# Revit family: SINK_PRIMARY
name_source: partatom
category: Furniture
units: mm (PartAtom-declared; Revit-internal decimal feet)

## family parameters
Always vertical = Yes
Cut with Voids When Loaded = No
OmniClass Number = 23.40.20.00
OmniClass Title = General Furniture and Specialties
Room Calculation Point = No
Shared = No
Work Plane-Based = No

## types (33) — shared parameters
FULL_WT = Yes
HEIGHT = 900 mm  [stored 2.95276 ft]
LOW_TAG = No
Manufacturer = IBR InnovaSystem
URL = https://ibr-innovasystem.com
zero-valued in all types: Default Elevation

## per-type parameters (varying)
| type | 1DOOR | 2DOOR | 3DOOR | ANCHO_FREG | DRBOWLW | DRBWL | DRBWR | DRNEUTW | DRNTL | DRNTR | Description | FRAMEW | FREG_CN | FREG_DC | FREG_IZ | HANDLEXB | HANDLEXN | POSBOWDRL | POSBOWDRR | POSNEUTL | POSNEUTR | POS_FREG | WIDTH | depth |
| SKPR-1575L | No | No | Yes | 500 mm  [stored 1.64042 ft] | 440 mm  [stored 1.44357 ft] | Yes | Yes | 587 mm | No | Yes | Primary Sink 1500x750, Bowl at Left side | 1468 mm  [stored 4.81627 ft] | No | No | Yes | 74 mm | 148 mm | 0 mm  [stored 0 ft] | 587 mm | 0 mm  [stored 0 ft] | 0 mm  [stored 0 ft] | 350 mm  [stored 1.14829 ft] | 1500 mm  [stored 4.92126 ft] | 750 mm  [stored 2.46063 ft] |
| SKPR-1575R | No | No | Yes | 500 mm  [stored 1.64042 ft] | 440 mm  [stored 1.44357 ft] | Yes | Yes | 587 mm | Yes | No | Primary Sink 1500x750, Bowl at Right side | 1468 mm  [stored 4.81627 ft] | No | Yes | No | 74 mm | 148 mm | 587 mm | 0 mm  [stored 0 ft] | 0 mm  [stored 0 ft] | 0 mm  [stored 0 ft] | 1150 mm | 1500 mm  [stored 4.92126 ft] | 750 mm  [stored 2.46063 ft] |
| SKPR-1575C | No | No | Yes | 500 mm  [stored 1.64042 ft] | 440 mm  [stored 1.44357 ft] | Yes | Yes | 587 mm | No | Yes | Primary Sink 1500x750, Bowl at Center | 1468 mm  [stored 4.81627 ft] | Yes | No | No | 74 mm | 148 mm | 0 mm  [stored 0 ft] | 0 mm  [stored 0 ft] | 440 mm  [stored 1.44357 ft] | 440 mm  [stored 1.44357 ft] | 750 mm  [stored 2.46063 ft] | 1500 mm  [stored 4.92126 ft] | 750 mm  [stored 2.46063 ft] |
| SKPR-1560R | No | No | Yes | 500 mm  [stored 1.64042 ft] | 440 mm  [stored 1.44357 ft] | Yes | Yes | 587 mm | Yes | No | Primary Sink 1500x600, Bowl at Right side | 1468 mm  [stored 4.81627 ft] | No | Yes | No | 74 mm | 148 mm | 587 mm | 0 mm  [stored 0 ft] | 0 mm  [stored 0 ft] | 0 mm  [stored 0 ft] | 1150 mm | 1500 mm  [stored 4.92126 ft] | 600 mm  [stored 1.9685 ft] |
| SKPR-1560L | No | No | Yes | 500 mm  [stored 1.64042 ft] | 440 mm  [stored 1.44357 ft] | Yes | Yes | 587 mm | No | Yes | Primary Sink 1500x600, Bowl at Left side | 1468 mm  [stored 4.81627 ft] | No | No | Yes | 74 mm | 148 mm | 0 mm  [stored 0 ft] | 587 mm | 0 mm  [stored 0 ft] | 0 mm  [stored 0 ft] | 350 mm  [stored 1.14829 ft] | 1500 mm  [stored 4.92126 ft] | 600 mm  [stored 1.9685 ft] |
| SKPR-1560C | No | No | Yes | 500 mm  [stored 1.64042 ft] | 440 mm  [stored 1.44357 ft] | Yes | Yes | 587 mm | No | Yes | Primary Sink 1500x600, Bowl at Center | 1468 mm  [stored 4.81627 ft] | Yes | No | No | 74 mm | 148 mm | 0 mm  [stored 0 ft] | 0 mm  [stored 0 ft] | 440 mm  [stored 1.44357 ft] | 440 mm  [stored 1.44357 ft] | 750 mm  [stored 2.46063 ft] | 1500 mm  [stored 4.92126 ft] | 600 mm  [stored 1.9685 ft] |
| SKPR-1590C | No | No | Yes | 500 mm  [stored 1.64042 ft] | 440 mm  [stored 1.44357 ft] | Yes | Yes | 587 mm | No | Yes | Primary Sink 1500x900, Bowl at Center | 1468 mm  [stored 4.81627 ft] | Yes | No | No | 74 mm | 148 mm | 0 mm  [stored 0 ft] | 0 mm  [stored 0 ft] | 440 mm  [stored 1.44357 ft] | 440 mm  [stored 1.44357 ft] | 750 mm  [stored 2.46063 ft] | 1500 mm  [stored 4.92126 ft] | 900 mm  [stored 2.95276 ft] |
| SKPR-1590L | No | No | Yes | 500 mm  [stored 1.64042 ft] | 440 mm  [stored 1.44357 ft] | Yes | Yes | 587 mm | No | Yes | Primary Sink 1500x900, Bowl at Left side | 1468 mm  [stored 4.81627 ft] | No | No | Yes | 74 mm | 148 mm | 0 mm  [stored 0 ft] | 587 mm | 0 mm  [stored 0 ft] | 0 mm  [stored 0 ft] | 350 mm  [stored 1.14829 ft] | 1500 mm  [stored 4.92126 ft] | 900 mm  [stored 2.95276 ft] |
| SKPR-1590R | No | No | Yes | 500 mm  [stored 1.64042 ft] | 440 mm  [stored 1.44357 ft] | Yes | Yes | 587 mm | Yes | No | Primary Sink 1500x900, Bowl at Right side | 1468 mm  [stored 4.81627 ft] | No | Yes | No | 74 mm | 148 mm | 587 mm | 0 mm  [stored 0 ft] | 0 mm  [stored 0 ft] | 0 mm  [stored 0 ft] | 1150 mm | 1500 mm  [stored 4.92126 ft] | 900 mm  [stored 2.95276 ft] |
| SKPR-1275L | No | Yes | No | 500 mm  [stored 1.64042 ft] | 584 mm  [stored 1.91601 ft] | Yes | Yes | 600 mm  [stored 1.9685 ft] | No | No | Primary Sink 1200x750, Bowl at Left side | 1168 mm  [stored 3.83202 ft] | No | No | Yes | 146 mm  [stored 0.479003 ft] | 154 mm  [stored 0.505249 ft] | 0 mm  [stored 0 ft] | 0 mm  [stored 0 ft] | 0 mm  [stored 0 ft] | 0 mm  [stored 0 ft] | 350 mm  [stored 1.14829 ft] | 1200 mm  [stored 3.93701 ft] | 750 mm  [stored 2.46063 ft] |
| SKPR-1275R | No | Yes | No | 500 mm  [stored 1.64042 ft] | 584 mm  [stored 1.91601 ft] | Yes | Yes | 600 mm  [stored 1.9685 ft] | No | No | Primary Sink 1200x750, Bowl at Right side | 1168 mm  [stored 3.83202 ft] | No | Yes | No | 146 mm  [stored 0.479003 ft] | 154 mm  [stored 0.505249 ft] | 0 mm  [stored 0 ft] | 0 mm  [stored 0 ft] | 0 mm  [stored 0 ft] | 0 mm  [stored 0 ft] | 850 mm  [stored 2.78871 ft] | 1200 mm  [stored 3.93701 ft] | 750 mm  [stored 2.46063 ft] |
| SKPR-1275C | No | Yes | No | 500 mm  [stored 1.64042 ft] | 584 mm  [stored 1.91601 ft] | Yes | Yes | 600 mm  [stored 1.9685 ft] | No | No | Primary Sink 1200x750, Bowl at Center | 1168 mm  [stored 3.83202 ft] | Yes | No | No | 146 mm  [stored 0.479003 ft] | 154 mm  [stored 0.505249 ft] | 0 mm  [stored 0 ft] | 0 mm  [stored 0 ft] | 0 mm  [stored 0 ft] | 0 mm  [stored 0 ft] | 600 mm  [stored 1.9685 ft] | 1200 mm  [stored 3.93701 ft] | 750 mm  [stored 2.46063 ft] |
| SKPR-1260C | No | Yes | No | 500 mm  [stored 1.64042 ft] | 584 mm  [stored 1.91601 ft] | Yes | Yes | 600 mm  [stored 1.9685 ft] | No | No | Primary Sink 1200x600, Bowl at Center | 1168 mm  [stored 3.83202 ft] | Yes | No | No | 146 mm  [stored 0.479003 ft] | 154 mm  [stored 0.505249 ft] | 0 mm  [stored 0 ft] | 0 mm  [stored 0 ft] | 0 mm  [stored 0 ft] | 0 mm  [stored 0 ft] | 600 mm  [stored 1.9685 ft] | 1200 mm  [stored 3.93701 ft] | 600 mm  [stored 1.9685 ft] |
| SKPR-1260L | No | Yes | No | 500 mm  [stored 1.64042 ft] | 584 mm  [stored 1.91601 ft] | Yes | Yes | 600 mm  [stored 1.9685 ft] | No | No | Primary Sink 1200x600, Bowl at Left side | 1168 mm  [stored 3.83202 ft] | No | No | Yes | 146 mm  [stored 0.479003 ft] | 154 mm  [stored 0.505249 ft] | 0 mm  [stored 0 ft] | 0 mm  [stored 0 ft] | 0 mm  [stored 0 ft] | 0 mm  [stored 0 ft] | 350 mm  [stored 1.14829 ft] | 1200 mm  [stored 3.93701 ft] | 600 mm  [stored 1.9685 ft] |
| SKPR-1260R | No | Yes | No | 500 mm  [stored 1.64042 ft] | 584 mm  [stored 1.91601 ft] | Yes | Yes | 600 mm  [stored 1.9685 ft] | No | No | Primary Sink 1200x600, Bowl at Right side | 1168 mm  [stored 3.83202 ft] | No | Yes | No | 146 mm  [stored 0.479003 ft] | 154 mm  [stored 0.505249 ft] | 0 mm  [stored 0 ft] | 0 mm  [stored 0 ft] | 0 mm  [stored 0 ft] | 0 mm  [stored 0 ft] | 850 mm  [stored 2.78871 ft] | 1200 mm  [stored 3.93701 ft] | 600 mm  [stored 1.9685 ft] |
| SKPR-1290R | No | Yes | No | 500 mm  [stored 1.64042 ft] | 584 mm  [stored 1.91601 ft] | Yes | Yes | 600 mm  [stored 1.9685 ft] | No | No | Primary Sink 1200x900, Bowl at Right side | 1168 mm  [stored 3.83202 ft] | No | Yes | No | 146 mm  [stored 0.479003 ft] | 154 mm  [stored 0.505249 ft] | 0 mm  [stored 0 ft] | 0 mm  [stored 0 ft] | 0 mm  [stored 0 ft] | 0 mm  [stored 0 ft] | 850 mm  [stored 2.78871 ft] | 1200 mm  [stored 3.93701 ft] | 900 mm  [stored 2.95276 ft] |
| SKPR-1290L | No | Yes | No | 500 mm  [stored 1.64042 ft] | 584 mm  [stored 1.91601 ft] | Yes | Yes | 600 mm  [stored 1.9685 ft] | No | No | Primary Sink 1200x900, Bowl at Left side | 1168 mm  [stored 3.83202 ft] | No | No | Yes | 146 mm  [stored 0.479003 ft] | 154 mm  [stored 0.505249 ft] | 0 mm  [stored 0 ft] | 0 mm  [stored 0 ft] | 0 mm  [stored 0 ft] | 0 mm  [stored 0 ft] | 350 mm  [stored 1.14829 ft] | 1200 mm  [stored 3.93701 ft] | 900 mm  [stored 2.95276 ft] |
| SKPR-1290C | No | Yes | No | 500 mm  [stored 1.64042 ft] | 584 mm  [stored 1.91601 ft] | Yes | Yes | 600 mm  [stored 1.9685 ft] | No | No | Primary Sink 1200x900, Bowl at Center | 1168 mm  [stored 3.83202 ft] | Yes | No | No | 146 mm  [stored 0.479003 ft] | 154 mm  [stored 0.505249 ft] | 0 mm  [stored 0 ft] | 0 mm  [stored 0 ft] | 0 mm  [stored 0 ft] | 0 mm  [stored 0 ft] | 600 mm  [stored 1.9685 ft] | 1200 mm  [stored 3.93701 ft] | 900 mm  [stored 2.95276 ft] |
| SKPR-0975R | No | Yes | No | 400 mm  [stored 1.31234 ft] | 434 mm  [stored 1.42388 ft] | Yes | Yes | 600 mm  [stored 1.9685 ft] | No | No | Primary Sink 900x750, Bowl at Right side | 868 mm  [stored 2.84777 ft] | No | Yes | No | 71 mm  [stored 0.23294 ft] | 154 mm  [stored 0.505249 ft] | 0 mm  [stored 0 ft] | 0 mm  [stored 0 ft] | 0 mm  [stored 0 ft] | 0 mm  [stored 0 ft] | 600 mm  [stored 1.9685 ft] | 900 mm  [stored 2.95276 ft] | 750 mm  [stored 2.46063 ft] |
| SKPR-0975L | No | Yes | No | 400 mm  [stored 1.31234 ft] | 434 mm  [stored 1.42388 ft] | Yes | Yes | 600 mm  [stored 1.9685 ft] | No | No | Primary Sink 900x750, Bowl at Left side | 868 mm  [stored 2.84777 ft] | No | No | Yes | 71 mm  [stored 0.23294 ft] | 154 mm  [stored 0.505249 ft] | 0 mm  [stored 0 ft] | 0 mm  [stored 0 ft] | 0 mm  [stored 0 ft] | 0 mm  [stored 0 ft] | 300 mm  [stored 0.984252 ft] | 900 mm  [stored 2.95276 ft] | 750 mm  [stored 2.46063 ft] |
| SKPR-0975C | No | Yes | No | 400 mm  [stored 1.31234 ft] | 434 mm  [stored 1.42388 ft] | Yes | Yes | 600 mm  [stored 1.9685 ft] | No | No | Primary Sink 900x750, Bowl at Center | 868 mm  [stored 2.84777 ft] | Yes | No | No | 71 mm  [stored 0.23294 ft] | 154 mm  [stored 0.505249 ft] | 0 mm  [stored 0 ft] | 0 mm  [stored 0 ft] | 0 mm  [stored 0 ft] | 0 mm  [stored 0 ft] | 450 mm  [stored 1.47638 ft] | 900 mm  [stored 2.95276 ft] | 750 mm  [stored 2.46063 ft] |
| SKPR-0960C | No | Yes | No | 400 mm  [stored 1.31234 ft] | 434 mm  [stored 1.42388 ft] | Yes | Yes | 600 mm  [stored 1.9685 ft] | No | No | Primary Sink 900x600, Bowl at Center | 868 mm  [stored 2.84777 ft] | Yes | No | No | 71 mm  [stored 0.23294 ft] | 154 mm  [stored 0.505249 ft] | 0 mm  [stored 0 ft] | 0 mm  [stored 0 ft] | 0 mm  [stored 0 ft] | 0 mm  [stored 0 ft] | 450 mm  [stored 1.47638 ft] | 900 mm  [stored 2.95276 ft] | 750 mm  [stored 2.46063 ft] |
| SKPR-0960R | No | Yes | No | 400 mm  [stored 1.31234 ft] | 434 mm  [stored 1.42388 ft] | Yes | Yes | 600 mm  [stored 1.9685 ft] | No | No | Primary Sink 900x600, Bowl at Right side | 868 mm  [stored 2.84777 ft] | No | Yes | No | 71 mm  [stored 0.23294 ft] | 154 mm  [stored 0.505249 ft] | 0 mm  [stored 0 ft] | 0 mm  [stored 0 ft] | 0 mm  [stored 0 ft] | 0 mm  [stored 0 ft] | 600 mm  [stored 1.9685 ft] | 900 mm  [stored 2.95276 ft] | 750 mm  [stored 2.46063 ft] |
| SKPR-0960L | No | Yes | No | 400 mm  [stored 1.31234 ft] | 434 mm  [stored 1.42388 ft] | Yes | Yes | 600 mm  [stored 1.9685 ft] | No | No | Primary Sink 900x600, Bowl at Left side | 868 mm  [stored 2.84777 ft] | No | No | Yes | 71 mm  [stored 0.23294 ft] | 154 mm  [stored 0.505249 ft] | 0 mm  [stored 0 ft] | 0 mm  [stored 0 ft] | 0 mm  [stored 0 ft] | 0 mm  [stored 0 ft] | 300 mm  [stored 0.984252 ft] | 900 mm  [stored 2.95276 ft] | 750 mm  [stored 2.46063 ft] |
| SKPR-0990L | No | Yes | No | 400 mm  [stored 1.31234 ft] | 434 mm  [stored 1.42388 ft] | Yes | Yes | 600 mm  [stored 1.9685 ft] | No | No | Primary Sink 900x900, Bowl at Left side | 868 mm  [stored 2.84777 ft] | No | No | Yes | 71 mm  [stored 0.23294 ft] | 154 mm  [stored 0.505249 ft] | 0 mm  [stored 0 ft] | 0 mm  [stored 0 ft] | 0 mm  [stored 0 ft] | 0 mm  [stored 0 ft] | 300 mm  [stored 0.984252 ft] | 900 mm  [stored 2.95276 ft] | 900 mm  [stored 2.95276 ft] |
| SKPR-0990R | No | Yes | No | 400 mm  [stored 1.31234 ft] | 434 mm  [stored 1.42388 ft] | Yes | Yes | 600 mm  [stored 1.9685 ft] | No | No | Primary Sink 900x900, Bowl at Right side | 868 mm  [stored 2.84777 ft] | No | Yes | No | 71 mm  [stored 0.23294 ft] | 154 mm  [stored 0.505249 ft] | 0 mm  [stored 0 ft] | 0 mm  [stored 0 ft] | 0 mm  [stored 0 ft] | 0 mm  [stored 0 ft] | 600 mm  [stored 1.9685 ft] | 900 mm  [stored 2.95276 ft] | 900 mm  [stored 2.95276 ft] |
| SKPR-0990C | No | Yes | No | 400 mm  [stored 1.31234 ft] | 434 mm  [stored 1.42388 ft] | Yes | Yes | 600 mm  [stored 1.9685 ft] | No | No | Primary Sink 900x900, Bowl at Center | 868 mm  [stored 2.84777 ft] | Yes | No | No | 71 mm  [stored 0.23294 ft] | 154 mm  [stored 0.505249 ft] | 0 mm  [stored 0 ft] | 0 mm  [stored 0 ft] | 0 mm  [stored 0 ft] | 0 mm  [stored 0 ft] | 450 mm  [stored 1.47638 ft] | 900 mm  [stored 2.95276 ft] | 900 mm  [stored 2.95276 ft] |
| SKPR-0675C-R | Yes | No | No | 400 mm  [stored 1.31234 ft] | 568 mm  [stored 1.86352 ft] | No | Yes | 600 mm  [stored 1.9685 ft] | No | No | Primary Sink 600x750, Bowl at Center, Right Opening Door | 568 mm  [stored 1.86352 ft] | No | Yes | No | 138 mm  [stored 0.452756 ft] | 154 mm  [stored 0.505249 ft] | 0 mm  [stored 0 ft] | 0 mm  [stored 0 ft] | 0 mm  [stored 0 ft] | 0 mm  [stored 0 ft] | 300 mm  [stored 0.984252 ft] | 600 mm  [stored 1.9685 ft] | 750 mm  [stored 2.46063 ft] |
| SKPR-0675C-L | Yes | No | No | 400 mm  [stored 1.31234 ft] | 568 mm  [stored 1.86352 ft] | Yes | No | 600 mm  [stored 1.9685 ft] | No | No | Primary Sink 600x750, Bowl at Center, Left Opening Door | 568 mm  [stored 1.86352 ft] | No | No | Yes | 138 mm  [stored 0.452756 ft] | 154 mm  [stored 0.505249 ft] | 0 mm  [stored 0 ft] | 0 mm  [stored 0 ft] | 0 mm  [stored 0 ft] | 0 mm  [stored 0 ft] | 300 mm  [stored 0.984252 ft] | 600 mm  [stored 1.9685 ft] | 750 mm  [stored 2.46063 ft] |
| SKPR-0660C-R | Yes | No | No | 400 mm  [stored 1.31234 ft] | 568 mm  [stored 1.86352 ft] | No | Yes | 600 mm  [stored 1.9685 ft] | No | No | Primary Sink 600x600, Bowl at Center, Right Opening Door | 568 mm  [stored 1.86352 ft] | No | Yes | No | 138 mm  [stored 0.452756 ft] | 154 mm  [stored 0.505249 ft] | 0 mm  [stored 0 ft] | 0 mm  [stored 0 ft] | 0 mm  [stored 0 ft] | 0 mm  [stored 0 ft] | 300 mm  [stored 0.984252 ft] | 600 mm  [stored 1.9685 ft] | 600 mm  [stored 1.9685 ft] |
| SKPR-0660C-L | Yes | No | No | 400 mm  [stored 1.31234 ft] | 568 mm  [stored 1.86352 ft] | Yes | No | 600 mm  [stored 1.9685 ft] | No | No | Primary Sink 600x600, Bowl at Center, Left Opening Door | 568 mm  [stored 1.86352 ft] | No | No | Yes | 138 mm  [stored 0.452756 ft] | 154 mm  [stored 0.505249 ft] | 0 mm  [stored 0 ft] | 0 mm  [stored 0 ft] | 0 mm  [stored 0 ft] | 0 mm  [stored 0 ft] | 300 mm  [stored 0.984252 ft] | 600 mm  [stored 1.9685 ft] | 600 mm  [stored 1.9685 ft] |
| SKPR-0690C-L | Yes | No | No | 400 mm  [stored 1.31234 ft] | 568 mm  [stored 1.86352 ft] | Yes | No | 600 mm  [stored 1.9685 ft] | No | No | Primary Sink 600x900, Bowl at Center, Left Opening Door | 568 mm  [stored 1.86352 ft] | No | No | Yes | 138 mm  [stored 0.452756 ft] | 154 mm  [stored 0.505249 ft] | 0 mm  [stored 0 ft] | 0 mm  [stored 0 ft] | 0 mm  [stored 0 ft] | 0 mm  [stored 0 ft] | 300 mm  [stored 0.984252 ft] | 600 mm  [stored 1.9685 ft] | 900 mm  [stored 2.95276 ft] |
| SKPR-0690C-R | Yes | No | No | 400 mm  [stored 1.31234 ft] | 568 mm  [stored 1.86352 ft] | No | Yes | 600 mm  [stored 1.9685 ft] | No | No | Primary Sink 600x900, Bowl at Center, Right Opening Door | 568 mm  [stored 1.86352 ft] | No | Yes | No | 138 mm  [stored 0.452756 ft] | 154 mm  [stored 0.505249 ft] | 0 mm  [stored 0 ft] | 0 mm  [stored 0 ft] | 0 mm  [stored 0 ft] | 0 mm  [stored 0 ft] | 300 mm  [stored 0.984252 ft] | 600 mm  [stored 1.9685 ft] | 900 mm  [stored 2.95276 ft] |

note: [stored X ft] marks values corroborated as IEEE doubles in the binary element streams (Revit-internal decimal feet)

## geometry (parser evidence)
native form markers: Sweep x37
no freeform markers — native parametric forms only
